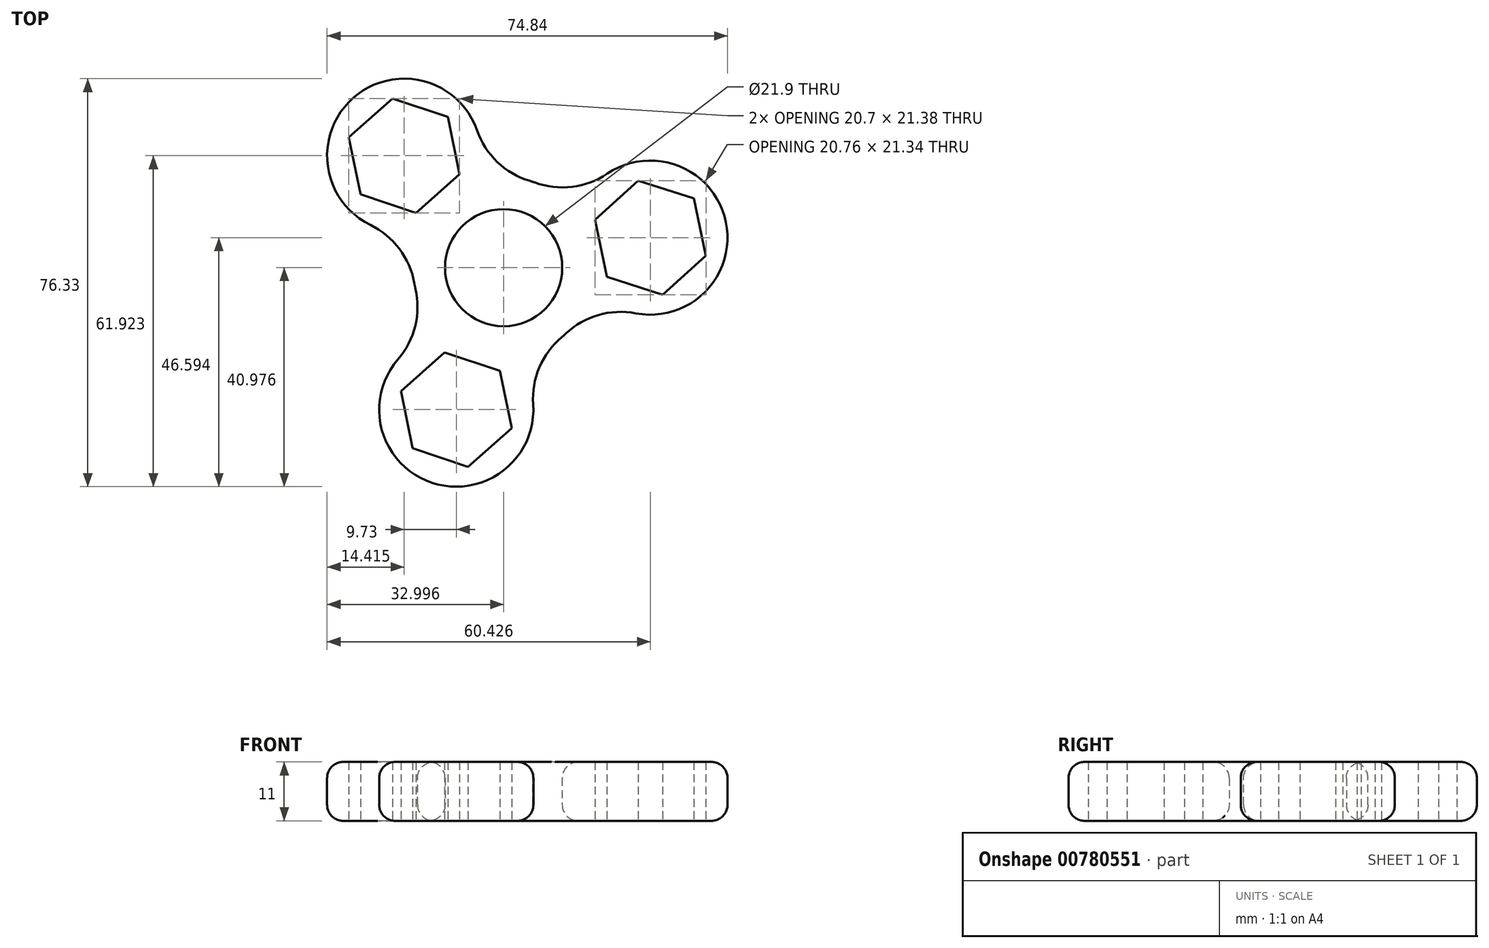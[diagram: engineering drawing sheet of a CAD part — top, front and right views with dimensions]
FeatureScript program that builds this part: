
annotation { "Feature Type Name" : "Feature", "Feature Type Description" : "" }
export const myFeature = defineFeature(function(context is Context, id is Id, definition is map)
    precondition{}
    {
        {
            var Q0;
            Q0=qCreatedBy(makeId("Top.planeOp"),FACE);
            var sketch = newSketch(context, id + "F0", { "sketchPlane" : qUnion([Q0])});
            skCircle(sketch, "E0", {"center": v(0.14, -0.37) * mm, "radius": 10.95 * mm});
            skCircle(sketch, "E1.0", {"center": v(0.14, -0.37) * mm, "radius": 16.95 * mm});
            skCircle(sketch, "E2.cCircle", {"center": v(0.14, -0.37) * mm, "radius": 14 * mm, "construction": true});
            skLineSegment(sketch, "E2.0", {"start": v(-18.44, 20.57) * mm, "end": v(27.57, 5.24) * mm, "construction": true});
            skLineSegment(sketch, "E2.1", {"start": v(27.57, 5.24) * mm, "end": v(-8.71, -26.94) * mm, "construction": true});
            skLineSegment(sketch, "E2.2", {"start": v(-8.71, -26.94) * mm, "end": v(-18.44, 20.57) * mm, "construction": true});
            skPoint(sketch, "E2.0.midPoint", {"position": v(4.56, 12.9) * mm});
            skCircle(sketch, "E3.cCircle", {"center": v(-18.44, 20.57) * mm, "radius": 9.45 * mm, "construction": true});
            skLineSegment(sketch, "E3.0", {"start": v(-28.8, 24.03) * mm, "end": v(-20.63, 31.26) * mm});
            skLineSegment(sketch, "E3.1", {"start": v(-20.63, 31.26) * mm, "end": v(-10.28, 27.8) * mm});
            skLineSegment(sketch, "E3.2", {"start": v(-10.28, 27.8) * mm, "end": v(-8.1, 17.12) * mm});
            skLineSegment(sketch, "E3.3", {"start": v(-8.1, 17.12) * mm, "end": v(-16.26, 9.88) * mm});
            skLineSegment(sketch, "E3.4", {"start": v(-16.26, 9.88) * mm, "end": v(-26.61, 13.34) * mm});
            skLineSegment(sketch, "E3.5", {"start": v(-26.61, 13.34) * mm, "end": v(-28.8, 24.03) * mm});
            skPoint(sketch, "E3.0.midPoint", {"position": v(-24.71, 27.65) * mm});
            skCircle(sketch, "E4.cCircle", {"center": v(27.57, 5.24) * mm, "radius": 9.45 * mm, "construction": true});
            skLineSegment(sketch, "E4.0", {"start": v(35.67, 12.55) * mm, "end": v(37.95, 1.88) * mm});
            skLineSegment(sketch, "E4.1", {"start": v(37.95, 1.88) * mm, "end": v(29.85, -5.43) * mm});
            skLineSegment(sketch, "E4.2", {"start": v(29.85, -5.43) * mm, "end": v(19.47, -2.07) * mm});
            skLineSegment(sketch, "E4.3", {"start": v(19.47, -2.07) * mm, "end": v(17.18, 8.6) * mm});
            skLineSegment(sketch, "E4.4", {"start": v(17.18, 8.6) * mm, "end": v(25.29, 15.91) * mm});
            skLineSegment(sketch, "E4.5", {"start": v(25.29, 15.91) * mm, "end": v(35.67, 12.55) * mm});
            skPoint(sketch, "E4.0.midPoint", {"position": v(36.8, 7.22) * mm});
            skCircle(sketch, "E5.cCircle", {"center": v(-8.71, -26.94) * mm, "radius": 9.45 * mm, "construction": true});
            skLineSegment(sketch, "E5.0", {"start": v(-6.53, -37.63) * mm, "end": v(-16.88, -34.17) * mm});
            skLineSegment(sketch, "E5.1", {"start": v(-16.88, -34.17) * mm, "end": v(-19.06, -23.48) * mm});
            skLineSegment(sketch, "E5.2", {"start": v(-19.06, -23.48) * mm, "end": v(-10.9, -16.25) * mm});
            skLineSegment(sketch, "E5.3", {"start": v(-10.9, -16.25) * mm, "end": v(-0.55, -19.7) * mm});
            skLineSegment(sketch, "E5.4", {"start": v(-0.55, -19.7) * mm, "end": v(1.63, -30.4) * mm});
            skLineSegment(sketch, "E5.5", {"start": v(1.63, -30.4) * mm, "end": v(-6.53, -37.63) * mm});
            skPoint(sketch, "E5.0.midPoint", {"position": v(-11.7, -35.9) * mm});
            skCircle(sketch, "E6", {"center": v(-8.71, -26.94) * mm, "radius": 14.41 * mm});
            skCircle(sketch, "E7", {"center": v(27.57, 5.24) * mm, "radius": 14.41 * mm});
            skCircle(sketch, "E8", {"center": v(-18.44, 20.57) * mm, "radius": 14.41 * mm});
            skPoint(sketch, "E9.endSnap0", {"position": v(-13.58, -3.18) * mm});
            skLineSegment(sketch, "E10", {"start": v(0.14, -0.37) * mm, "end": v(51.26, 10.11) * mm, "construction": true});
            skLineSegment(sketch, "E11", {"start": v(0.14, -0.37) * mm, "end": v(-32.46, 36.46) * mm, "construction": true});
            skLineSegment(sketch, "E12", {"start": v(0.14, -0.37) * mm, "end": v(-11.7, -35.9) * mm, "construction": true});
            skPoint(sketch, "E13.trimOffspring.end.orphan", {"position": v(-13.58, 9.59) * mm});
            skSolve(sketch);
        }
        {
            var Q0;
            Q0=qSketchRegion(id+"F0",true);
            extrude(context, id + "F1", {"entities" : qUnion([Q0]), "depth" : 11 * mm, "offsetDistance" : 25 * mm});
        }
        {
            var Q0;
            {var subQ0=sQuery(id+"F0.wireOp",EDGE,"E7");var subQ1=sQuery(id+"F0.wireOp",EDGE,"E1.0");Q0=makeQuery(id+"F1.opExtrude","SWEPT_EDGE",EDGE,{"disambiguationData":[OSD([subQ1,subQ0]),TDD([makeQuery(id+"F0.imprint","INTERSECT",VERTEX,{"disambiguationData":[OD(1.0)],"derivedFrom":[subQ1,subQ0]})])]});}
            var Q1;
            {var subQ0=sQuery(id+"F0.wireOp",EDGE,"E6");var subQ1=sQuery(id+"F0.wireOp",EDGE,"E1.0");Q1=makeQuery(id+"F1.opExtrude","SWEPT_EDGE",EDGE,{"disambiguationData":[OSD([subQ1,subQ0]),TDD([makeQuery(id+"F0.imprint","INTERSECT",VERTEX,{"disambiguationData":[OD(1.0)],"derivedFrom":[subQ1,subQ0]})])]});}
            var Q2;
            {var subQ0=sQuery(id+"F0.wireOp",EDGE,"E6");var subQ1=sQuery(id+"F0.wireOp",EDGE,"E1.0");Q2=makeQuery(id+"F1.opExtrude","SWEPT_EDGE",EDGE,{"disambiguationData":[OSD([subQ1,subQ0]),TDD([makeQuery(id+"F0.imprint","INTERSECT",VERTEX,{"disambiguationData":[OD(0.0)],"derivedFrom":[subQ1,subQ0]})])]});}
            var Q3;
            {var subQ0=sQuery(id+"F0.wireOp",EDGE,"E8");var subQ1=sQuery(id+"F0.wireOp",EDGE,"E1.0");Q3=makeQuery(id+"F1.opExtrude","SWEPT_EDGE",EDGE,{"disambiguationData":[OSD([subQ1,subQ0]),TDD([makeQuery(id+"F0.imprint","INTERSECT",VERTEX,{"disambiguationData":[OD(1.0)],"derivedFrom":[subQ1,subQ0]})])]});}
            var Q4;
            {var subQ0=sQuery(id+"F0.wireOp",EDGE,"E8");var subQ1=sQuery(id+"F0.wireOp",EDGE,"E1.0");Q4=makeQuery(id+"F1.opExtrude","SWEPT_EDGE",EDGE,{"disambiguationData":[OSD([subQ1,subQ0]),TDD([makeQuery(id+"F0.imprint","INTERSECT",VERTEX,{"disambiguationData":[OD(0.0)],"derivedFrom":[subQ1,subQ0]})])]});}
            var Q5;
            {var subQ0=sQuery(id+"F0.wireOp",EDGE,"E7");var subQ1=sQuery(id+"F0.wireOp",EDGE,"E1.0");Q5=makeQuery(id+"F1.opExtrude","SWEPT_EDGE",EDGE,{"disambiguationData":[OSD([subQ1,subQ0]),TDD([makeQuery(id+"F0.imprint","INTERSECT",VERTEX,{"disambiguationData":[OD(0.0)],"derivedFrom":[subQ1,subQ0]})])]});}
            fillet(context, id + "F2", {"entities" : qUnion([Q0, Q1, Q2, Q3, Q4, Q5]), "radius" : 15 * mm, "tangentPropagation" : true, "allowEdgeOverflow" : false});
        }
        {
            var Q0;
            Q0=makeQuery(id+"F1.opExtrude","CAP_EDGE",EDGE,{"disambiguationData":[OSD([sQuery(id+"F0.wireOp",EDGE,"E8")])],"isStart":true});
            var Q1;
            Q1=makeQuery(id+"F1.opExtrude","CAP_EDGE",EDGE,{"disambiguationData":[OSD([sQuery(id+"F0.wireOp",EDGE,"E7")])],"isStart":true});
            var Q2;
            {var subQ0=sQuery(id+"F0.wireOp",EDGE,"E6");var subQ1=sQuery(id+"F0.wireOp",EDGE,"E1.0");Q2=makeQuery(id+"F2.opFillet","BLEND_EDGE",EDGE,{"blendedFrom":[makeQuery(id+"F1.opExtrude","SWEPT_EDGE",EDGE,{"disambiguationData":[OSD([subQ1,subQ0]),TDD([makeQuery(id+"F0.imprint","INTERSECT",VERTEX,{"disambiguationData":[OD(1.0)],"derivedFrom":[subQ1,subQ0]})])]}),makeQuery(id+"F1.opExtrude","CAP_FACE",FACE,{"disambiguationData":[OSD([sQuery(id+"F0.wireOp",EDGE,"E0"),subQ1,sQuery(id+"F0.wireOp",EDGE,"E3.0"),sQuery(id+"F0.wireOp",EDGE,"E3.1"),sQuery(id+"F0.wireOp",EDGE,"E3.2"),sQuery(id+"F0.wireOp",EDGE,"E3.3"),sQuery(id+"F0.wireOp",EDGE,"E3.4"),sQuery(id+"F0.wireOp",EDGE,"E3.5"),sQuery(id+"F0.wireOp",EDGE,"E4.0"),sQuery(id+"F0.wireOp",EDGE,"E4.1"),sQuery(id+"F0.wireOp",EDGE,"E4.2"),sQuery(id+"F0.wireOp",EDGE,"E4.3"),sQuery(id+"F0.wireOp",EDGE,"E4.4"),sQuery(id+"F0.wireOp",EDGE,"E4.5"),sQuery(id+"F0.wireOp",EDGE,"E5.0"),sQuery(id+"F0.wireOp",EDGE,"E5.1"),sQuery(id+"F0.wireOp",EDGE,"E5.2"),sQuery(id+"F0.wireOp",EDGE,"E5.3"),sQuery(id+"F0.wireOp",EDGE,"E5.4"),sQuery(id+"F0.wireOp",EDGE,"E5.5"),subQ0,sQuery(id+"F0.wireOp",EDGE,"E7"),sQuery(id+"F0.wireOp",EDGE,"E8")])],"isStart":true})],"blendedInto":[makeQuery(id+"F1.opExtrude","CAP_FACE",FACE,{"disambiguationData":[OSD([sQuery(id+"F0.wireOp",EDGE,"E0"),subQ1,sQuery(id+"F0.wireOp",EDGE,"E3.0"),sQuery(id+"F0.wireOp",EDGE,"E3.1"),sQuery(id+"F0.wireOp",EDGE,"E3.2"),sQuery(id+"F0.wireOp",EDGE,"E3.3"),sQuery(id+"F0.wireOp",EDGE,"E3.4"),sQuery(id+"F0.wireOp",EDGE,"E3.5"),sQuery(id+"F0.wireOp",EDGE,"E4.0"),sQuery(id+"F0.wireOp",EDGE,"E4.1"),sQuery(id+"F0.wireOp",EDGE,"E4.2"),sQuery(id+"F0.wireOp",EDGE,"E4.3"),sQuery(id+"F0.wireOp",EDGE,"E4.4"),sQuery(id+"F0.wireOp",EDGE,"E4.5"),sQuery(id+"F0.wireOp",EDGE,"E5.0"),sQuery(id+"F0.wireOp",EDGE,"E5.1"),sQuery(id+"F0.wireOp",EDGE,"E5.2"),sQuery(id+"F0.wireOp",EDGE,"E5.3"),sQuery(id+"F0.wireOp",EDGE,"E5.4"),sQuery(id+"F0.wireOp",EDGE,"E5.5"),subQ0,sQuery(id+"F0.wireOp",EDGE,"E7"),sQuery(id+"F0.wireOp",EDGE,"E8")])],"isStart":true})]});}
            fillet(context, id + "F3", {"entities" : qUnion([Q0, Q1, Q2]), "radius" : 3 * mm, "tangentPropagation" : true, "allowEdgeOverflow" : false});
        }
        {
            var Q0;
            {var subQ0=sQuery(id+"F0.wireOp",EDGE,"E6");var subQ1=sQuery(id+"F0.wireOp",EDGE,"E1.0");Q0=makeQuery(id+"F2.opFillet","BLEND_EDGE",EDGE,{"blendedFrom":[makeQuery(id+"F1.opExtrude","SWEPT_EDGE",EDGE,{"disambiguationData":[OSD([subQ1,subQ0]),TDD([makeQuery(id+"F0.imprint","INTERSECT",VERTEX,{"disambiguationData":[OD(0.0)],"derivedFrom":[subQ1,subQ0]})])]}),makeQuery(id+"F1.opExtrude","CAP_FACE",FACE,{"disambiguationData":[OSD([sQuery(id+"F0.wireOp",EDGE,"E0"),subQ1,sQuery(id+"F0.wireOp",EDGE,"E3.0"),sQuery(id+"F0.wireOp",EDGE,"E3.1"),sQuery(id+"F0.wireOp",EDGE,"E3.2"),sQuery(id+"F0.wireOp",EDGE,"E3.3"),sQuery(id+"F0.wireOp",EDGE,"E3.4"),sQuery(id+"F0.wireOp",EDGE,"E3.5"),sQuery(id+"F0.wireOp",EDGE,"E4.0"),sQuery(id+"F0.wireOp",EDGE,"E4.1"),sQuery(id+"F0.wireOp",EDGE,"E4.2"),sQuery(id+"F0.wireOp",EDGE,"E4.3"),sQuery(id+"F0.wireOp",EDGE,"E4.4"),sQuery(id+"F0.wireOp",EDGE,"E4.5"),sQuery(id+"F0.wireOp",EDGE,"E5.0"),sQuery(id+"F0.wireOp",EDGE,"E5.1"),sQuery(id+"F0.wireOp",EDGE,"E5.2"),sQuery(id+"F0.wireOp",EDGE,"E5.3"),sQuery(id+"F0.wireOp",EDGE,"E5.4"),sQuery(id+"F0.wireOp",EDGE,"E5.5"),subQ0,sQuery(id+"F0.wireOp",EDGE,"E7"),sQuery(id+"F0.wireOp",EDGE,"E8")])],"isStart":false})],"blendedInto":[makeQuery(id+"F1.opExtrude","CAP_FACE",FACE,{"disambiguationData":[OSD([sQuery(id+"F0.wireOp",EDGE,"E0"),subQ1,sQuery(id+"F0.wireOp",EDGE,"E3.0"),sQuery(id+"F0.wireOp",EDGE,"E3.1"),sQuery(id+"F0.wireOp",EDGE,"E3.2"),sQuery(id+"F0.wireOp",EDGE,"E3.3"),sQuery(id+"F0.wireOp",EDGE,"E3.4"),sQuery(id+"F0.wireOp",EDGE,"E3.5"),sQuery(id+"F0.wireOp",EDGE,"E4.0"),sQuery(id+"F0.wireOp",EDGE,"E4.1"),sQuery(id+"F0.wireOp",EDGE,"E4.2"),sQuery(id+"F0.wireOp",EDGE,"E4.3"),sQuery(id+"F0.wireOp",EDGE,"E4.4"),sQuery(id+"F0.wireOp",EDGE,"E4.5"),sQuery(id+"F0.wireOp",EDGE,"E5.0"),sQuery(id+"F0.wireOp",EDGE,"E5.1"),sQuery(id+"F0.wireOp",EDGE,"E5.2"),sQuery(id+"F0.wireOp",EDGE,"E5.3"),sQuery(id+"F0.wireOp",EDGE,"E5.4"),sQuery(id+"F0.wireOp",EDGE,"E5.5"),subQ0,sQuery(id+"F0.wireOp",EDGE,"E7"),sQuery(id+"F0.wireOp",EDGE,"E8")])],"isStart":false})]});}
            var Q1;
            Q1=makeQuery(id+"F1.opExtrude","CAP_EDGE",EDGE,{"disambiguationData":[OSD([sQuery(id+"F0.wireOp",EDGE,"E6")])],"isStart":false});
            var Q2;
            {var subQ0=sQuery(id+"F0.wireOp",EDGE,"E6");var subQ1=sQuery(id+"F0.wireOp",EDGE,"E1.0");Q2=makeQuery(id+"F2.opFillet","BLEND_EDGE",EDGE,{"blendedFrom":[makeQuery(id+"F1.opExtrude","SWEPT_EDGE",EDGE,{"disambiguationData":[OSD([subQ1,subQ0]),TDD([makeQuery(id+"F0.imprint","INTERSECT",VERTEX,{"disambiguationData":[OD(1.0)],"derivedFrom":[subQ1,subQ0]})])]}),makeQuery(id+"F1.opExtrude","CAP_FACE",FACE,{"disambiguationData":[OSD([sQuery(id+"F0.wireOp",EDGE,"E0"),subQ1,sQuery(id+"F0.wireOp",EDGE,"E3.0"),sQuery(id+"F0.wireOp",EDGE,"E3.1"),sQuery(id+"F0.wireOp",EDGE,"E3.2"),sQuery(id+"F0.wireOp",EDGE,"E3.3"),sQuery(id+"F0.wireOp",EDGE,"E3.4"),sQuery(id+"F0.wireOp",EDGE,"E3.5"),sQuery(id+"F0.wireOp",EDGE,"E4.0"),sQuery(id+"F0.wireOp",EDGE,"E4.1"),sQuery(id+"F0.wireOp",EDGE,"E4.2"),sQuery(id+"F0.wireOp",EDGE,"E4.3"),sQuery(id+"F0.wireOp",EDGE,"E4.4"),sQuery(id+"F0.wireOp",EDGE,"E4.5"),sQuery(id+"F0.wireOp",EDGE,"E5.0"),sQuery(id+"F0.wireOp",EDGE,"E5.1"),sQuery(id+"F0.wireOp",EDGE,"E5.2"),sQuery(id+"F0.wireOp",EDGE,"E5.3"),sQuery(id+"F0.wireOp",EDGE,"E5.4"),sQuery(id+"F0.wireOp",EDGE,"E5.5"),subQ0,sQuery(id+"F0.wireOp",EDGE,"E7"),sQuery(id+"F0.wireOp",EDGE,"E8")])],"isStart":false})],"blendedInto":[makeQuery(id+"F1.opExtrude","CAP_FACE",FACE,{"disambiguationData":[OSD([sQuery(id+"F0.wireOp",EDGE,"E0"),subQ1,sQuery(id+"F0.wireOp",EDGE,"E3.0"),sQuery(id+"F0.wireOp",EDGE,"E3.1"),sQuery(id+"F0.wireOp",EDGE,"E3.2"),sQuery(id+"F0.wireOp",EDGE,"E3.3"),sQuery(id+"F0.wireOp",EDGE,"E3.4"),sQuery(id+"F0.wireOp",EDGE,"E3.5"),sQuery(id+"F0.wireOp",EDGE,"E4.0"),sQuery(id+"F0.wireOp",EDGE,"E4.1"),sQuery(id+"F0.wireOp",EDGE,"E4.2"),sQuery(id+"F0.wireOp",EDGE,"E4.3"),sQuery(id+"F0.wireOp",EDGE,"E4.4"),sQuery(id+"F0.wireOp",EDGE,"E4.5"),sQuery(id+"F0.wireOp",EDGE,"E5.0"),sQuery(id+"F0.wireOp",EDGE,"E5.1"),sQuery(id+"F0.wireOp",EDGE,"E5.2"),sQuery(id+"F0.wireOp",EDGE,"E5.3"),sQuery(id+"F0.wireOp",EDGE,"E5.4"),sQuery(id+"F0.wireOp",EDGE,"E5.5"),subQ0,sQuery(id+"F0.wireOp",EDGE,"E7"),sQuery(id+"F0.wireOp",EDGE,"E8")])],"isStart":false})]});}
            var Q3;
            {var subQ0=sQuery(id+"F0.wireOp",EDGE,"E7");var subQ1=sQuery(id+"F0.wireOp",EDGE,"E1.0");Q3=makeQuery(id+"F2.opFillet","BLEND_EDGE",EDGE,{"blendedFrom":[makeQuery(id+"F1.opExtrude","SWEPT_EDGE",EDGE,{"disambiguationData":[OSD([subQ1,subQ0]),TDD([makeQuery(id+"F0.imprint","INTERSECT",VERTEX,{"disambiguationData":[OD(1.0)],"derivedFrom":[subQ1,subQ0]})])]}),makeQuery(id+"F1.opExtrude","CAP_FACE",FACE,{"disambiguationData":[OSD([sQuery(id+"F0.wireOp",EDGE,"E0"),subQ1,sQuery(id+"F0.wireOp",EDGE,"E3.0"),sQuery(id+"F0.wireOp",EDGE,"E3.1"),sQuery(id+"F0.wireOp",EDGE,"E3.2"),sQuery(id+"F0.wireOp",EDGE,"E3.3"),sQuery(id+"F0.wireOp",EDGE,"E3.4"),sQuery(id+"F0.wireOp",EDGE,"E3.5"),sQuery(id+"F0.wireOp",EDGE,"E4.0"),sQuery(id+"F0.wireOp",EDGE,"E4.1"),sQuery(id+"F0.wireOp",EDGE,"E4.2"),sQuery(id+"F0.wireOp",EDGE,"E4.3"),sQuery(id+"F0.wireOp",EDGE,"E4.4"),sQuery(id+"F0.wireOp",EDGE,"E4.5"),sQuery(id+"F0.wireOp",EDGE,"E5.0"),sQuery(id+"F0.wireOp",EDGE,"E5.1"),sQuery(id+"F0.wireOp",EDGE,"E5.2"),sQuery(id+"F0.wireOp",EDGE,"E5.3"),sQuery(id+"F0.wireOp",EDGE,"E5.4"),sQuery(id+"F0.wireOp",EDGE,"E5.5"),sQuery(id+"F0.wireOp",EDGE,"E6"),subQ0,sQuery(id+"F0.wireOp",EDGE,"E8")])],"isStart":false})],"blendedInto":[makeQuery(id+"F1.opExtrude","CAP_FACE",FACE,{"disambiguationData":[OSD([sQuery(id+"F0.wireOp",EDGE,"E0"),subQ1,sQuery(id+"F0.wireOp",EDGE,"E3.0"),sQuery(id+"F0.wireOp",EDGE,"E3.1"),sQuery(id+"F0.wireOp",EDGE,"E3.2"),sQuery(id+"F0.wireOp",EDGE,"E3.3"),sQuery(id+"F0.wireOp",EDGE,"E3.4"),sQuery(id+"F0.wireOp",EDGE,"E3.5"),sQuery(id+"F0.wireOp",EDGE,"E4.0"),sQuery(id+"F0.wireOp",EDGE,"E4.1"),sQuery(id+"F0.wireOp",EDGE,"E4.2"),sQuery(id+"F0.wireOp",EDGE,"E4.3"),sQuery(id+"F0.wireOp",EDGE,"E4.4"),sQuery(id+"F0.wireOp",EDGE,"E4.5"),sQuery(id+"F0.wireOp",EDGE,"E5.0"),sQuery(id+"F0.wireOp",EDGE,"E5.1"),sQuery(id+"F0.wireOp",EDGE,"E5.2"),sQuery(id+"F0.wireOp",EDGE,"E5.3"),sQuery(id+"F0.wireOp",EDGE,"E5.4"),sQuery(id+"F0.wireOp",EDGE,"E5.5"),sQuery(id+"F0.wireOp",EDGE,"E6"),subQ0,sQuery(id+"F0.wireOp",EDGE,"E8")])],"isStart":false})]});}
            var Q4;
            Q4=makeQuery(id+"F1.opExtrude","CAP_EDGE",EDGE,{"disambiguationData":[OSD([sQuery(id+"F0.wireOp",EDGE,"E7")])],"isStart":false});
            var Q5;
            {var subQ0=sQuery(id+"F0.wireOp",EDGE,"E7");var subQ1=sQuery(id+"F0.wireOp",EDGE,"E1.0");Q5=makeQuery(id+"F2.opFillet","BLEND_EDGE",EDGE,{"blendedFrom":[makeQuery(id+"F1.opExtrude","SWEPT_EDGE",EDGE,{"disambiguationData":[OSD([subQ1,subQ0]),TDD([makeQuery(id+"F0.imprint","INTERSECT",VERTEX,{"disambiguationData":[OD(0.0)],"derivedFrom":[subQ1,subQ0]})])]}),makeQuery(id+"F1.opExtrude","CAP_FACE",FACE,{"disambiguationData":[OSD([sQuery(id+"F0.wireOp",EDGE,"E0"),subQ1,sQuery(id+"F0.wireOp",EDGE,"E3.0"),sQuery(id+"F0.wireOp",EDGE,"E3.1"),sQuery(id+"F0.wireOp",EDGE,"E3.2"),sQuery(id+"F0.wireOp",EDGE,"E3.3"),sQuery(id+"F0.wireOp",EDGE,"E3.4"),sQuery(id+"F0.wireOp",EDGE,"E3.5"),sQuery(id+"F0.wireOp",EDGE,"E4.0"),sQuery(id+"F0.wireOp",EDGE,"E4.1"),sQuery(id+"F0.wireOp",EDGE,"E4.2"),sQuery(id+"F0.wireOp",EDGE,"E4.3"),sQuery(id+"F0.wireOp",EDGE,"E4.4"),sQuery(id+"F0.wireOp",EDGE,"E4.5"),sQuery(id+"F0.wireOp",EDGE,"E5.0"),sQuery(id+"F0.wireOp",EDGE,"E5.1"),sQuery(id+"F0.wireOp",EDGE,"E5.2"),sQuery(id+"F0.wireOp",EDGE,"E5.3"),sQuery(id+"F0.wireOp",EDGE,"E5.4"),sQuery(id+"F0.wireOp",EDGE,"E5.5"),sQuery(id+"F0.wireOp",EDGE,"E6"),subQ0,sQuery(id+"F0.wireOp",EDGE,"E8")])],"isStart":false})],"blendedInto":[makeQuery(id+"F1.opExtrude","CAP_FACE",FACE,{"disambiguationData":[OSD([sQuery(id+"F0.wireOp",EDGE,"E0"),subQ1,sQuery(id+"F0.wireOp",EDGE,"E3.0"),sQuery(id+"F0.wireOp",EDGE,"E3.1"),sQuery(id+"F0.wireOp",EDGE,"E3.2"),sQuery(id+"F0.wireOp",EDGE,"E3.3"),sQuery(id+"F0.wireOp",EDGE,"E3.4"),sQuery(id+"F0.wireOp",EDGE,"E3.5"),sQuery(id+"F0.wireOp",EDGE,"E4.0"),sQuery(id+"F0.wireOp",EDGE,"E4.1"),sQuery(id+"F0.wireOp",EDGE,"E4.2"),sQuery(id+"F0.wireOp",EDGE,"E4.3"),sQuery(id+"F0.wireOp",EDGE,"E4.4"),sQuery(id+"F0.wireOp",EDGE,"E4.5"),sQuery(id+"F0.wireOp",EDGE,"E5.0"),sQuery(id+"F0.wireOp",EDGE,"E5.1"),sQuery(id+"F0.wireOp",EDGE,"E5.2"),sQuery(id+"F0.wireOp",EDGE,"E5.3"),sQuery(id+"F0.wireOp",EDGE,"E5.4"),sQuery(id+"F0.wireOp",EDGE,"E5.5"),sQuery(id+"F0.wireOp",EDGE,"E6"),subQ0,sQuery(id+"F0.wireOp",EDGE,"E8")])],"isStart":false})]});}
            var Q6;
            {var subQ0=sQuery(id+"F0.wireOp",EDGE,"E8");var subQ1=sQuery(id+"F0.wireOp",EDGE,"E1.0");Q6=makeQuery(id+"F2.opFillet","BLEND_EDGE",EDGE,{"blendedFrom":[makeQuery(id+"F1.opExtrude","SWEPT_EDGE",EDGE,{"disambiguationData":[OSD([subQ1,subQ0]),TDD([makeQuery(id+"F0.imprint","INTERSECT",VERTEX,{"disambiguationData":[OD(0.0)],"derivedFrom":[subQ1,subQ0]})])]}),makeQuery(id+"F1.opExtrude","CAP_FACE",FACE,{"disambiguationData":[OSD([sQuery(id+"F0.wireOp",EDGE,"E0"),subQ1,sQuery(id+"F0.wireOp",EDGE,"E3.0"),sQuery(id+"F0.wireOp",EDGE,"E3.1"),sQuery(id+"F0.wireOp",EDGE,"E3.2"),sQuery(id+"F0.wireOp",EDGE,"E3.3"),sQuery(id+"F0.wireOp",EDGE,"E3.4"),sQuery(id+"F0.wireOp",EDGE,"E3.5"),sQuery(id+"F0.wireOp",EDGE,"E4.0"),sQuery(id+"F0.wireOp",EDGE,"E4.1"),sQuery(id+"F0.wireOp",EDGE,"E4.2"),sQuery(id+"F0.wireOp",EDGE,"E4.3"),sQuery(id+"F0.wireOp",EDGE,"E4.4"),sQuery(id+"F0.wireOp",EDGE,"E4.5"),sQuery(id+"F0.wireOp",EDGE,"E5.0"),sQuery(id+"F0.wireOp",EDGE,"E5.1"),sQuery(id+"F0.wireOp",EDGE,"E5.2"),sQuery(id+"F0.wireOp",EDGE,"E5.3"),sQuery(id+"F0.wireOp",EDGE,"E5.4"),sQuery(id+"F0.wireOp",EDGE,"E5.5"),sQuery(id+"F0.wireOp",EDGE,"E6"),sQuery(id+"F0.wireOp",EDGE,"E7"),subQ0])],"isStart":false})],"blendedInto":[makeQuery(id+"F1.opExtrude","CAP_FACE",FACE,{"disambiguationData":[OSD([sQuery(id+"F0.wireOp",EDGE,"E0"),subQ1,sQuery(id+"F0.wireOp",EDGE,"E3.0"),sQuery(id+"F0.wireOp",EDGE,"E3.1"),sQuery(id+"F0.wireOp",EDGE,"E3.2"),sQuery(id+"F0.wireOp",EDGE,"E3.3"),sQuery(id+"F0.wireOp",EDGE,"E3.4"),sQuery(id+"F0.wireOp",EDGE,"E3.5"),sQuery(id+"F0.wireOp",EDGE,"E4.0"),sQuery(id+"F0.wireOp",EDGE,"E4.1"),sQuery(id+"F0.wireOp",EDGE,"E4.2"),sQuery(id+"F0.wireOp",EDGE,"E4.3"),sQuery(id+"F0.wireOp",EDGE,"E4.4"),sQuery(id+"F0.wireOp",EDGE,"E4.5"),sQuery(id+"F0.wireOp",EDGE,"E5.0"),sQuery(id+"F0.wireOp",EDGE,"E5.1"),sQuery(id+"F0.wireOp",EDGE,"E5.2"),sQuery(id+"F0.wireOp",EDGE,"E5.3"),sQuery(id+"F0.wireOp",EDGE,"E5.4"),sQuery(id+"F0.wireOp",EDGE,"E5.5"),sQuery(id+"F0.wireOp",EDGE,"E6"),sQuery(id+"F0.wireOp",EDGE,"E7"),subQ0])],"isStart":false})]});}
            fillet(context, id + "F4", {"entities" : qUnion([Q0, Q1, Q2, Q3, Q4, Q5, Q6]), "radius" : 3 * mm, "tangentPropagation" : true, "allowEdgeOverflow" : false});
        }
        {
            var Q0;
            Q0=makeQuery(id+"F1.opExtrude","CAP_EDGE",EDGE,{"disambiguationData":[OSD([sQuery(id+"F0.wireOp",EDGE,"E0")])],"isStart":false});
            var Q1;
            Q1=makeQuery(id+"F1.opExtrude","CAP_EDGE",EDGE,{"disambiguationData":[OSD([sQuery(id+"F0.wireOp",EDGE,"E0")])],"isStart":true});
            fillet(context, id + "F5", {"entities" : qUnion([Q0, Q1]), "radius" : 3 * mm, "tangentPropagation" : true, "allowEdgeOverflow" : false});
        }
    });
